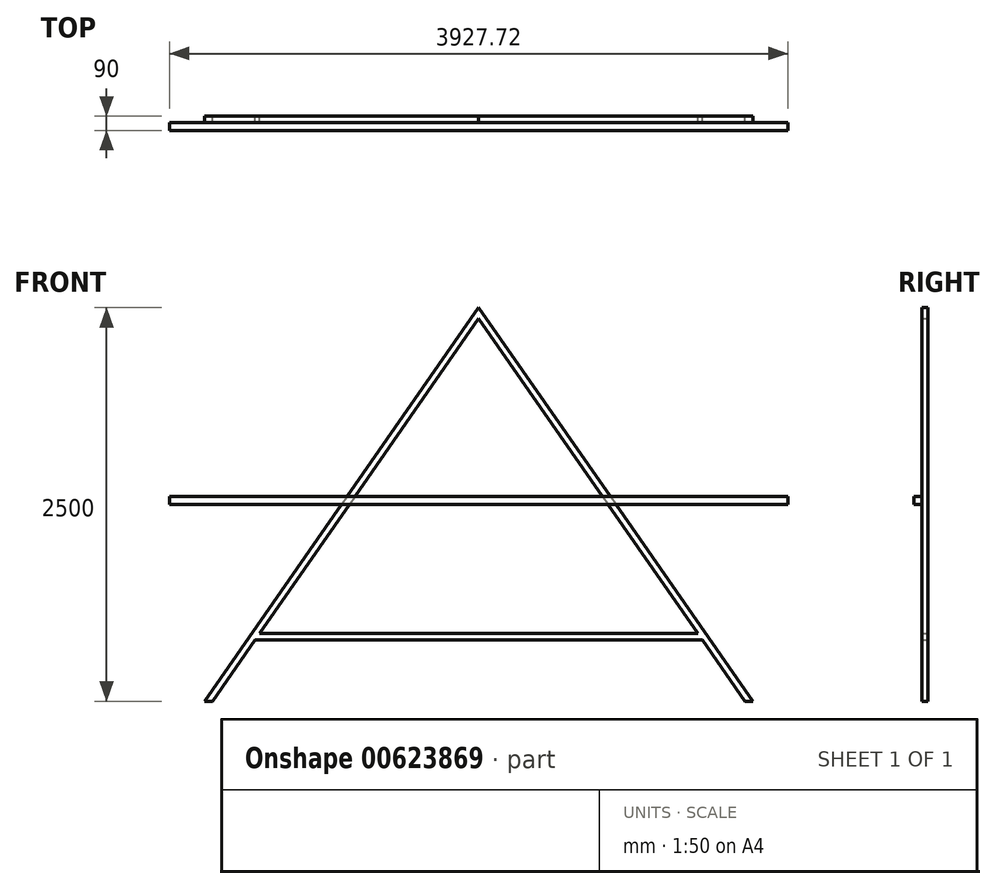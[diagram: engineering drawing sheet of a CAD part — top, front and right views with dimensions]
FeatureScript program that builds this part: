
annotation { "Feature Type Name" : "Feature", "Feature Type Description" : "" }
export const myFeature = defineFeature(function(context is Context, id is Id, definition is map)
    precondition{}
    {
        {
            var Q0;
            Q0=qCreatedBy(makeId("Front.planeOp"),FACE);
            var sketch = newSketch(context, id + "F0", { "sketchPlane" : qUnion([Q0])});
            skLineSegment(sketch, "E0", {"start": v(0, 2500) * mm, "end": v(-1740.78, 0) * mm});
            skLineSegment(sketch, "E1", {"start": v(0, 2500) * mm, "end": v(0, 2430) * mm});
            skLineSegment(sketch, "E2", {"start": v(0, 2430) * mm, "end": v(-1692.03, 0) * mm});
            skLineSegment(sketch, "E3", {"start": v(-1692.03, 0) * mm, "end": v(-1740.78, 0) * mm});
            skLineSegment(sketch, "E4.MirrorCS", {"start": v(1692.03, 0) * mm, "end": v(1740.78, 0) * mm});
            skLineSegment(sketch, "E5.MirrorCS", {"start": v(0, 2500) * mm, "end": v(1740.78, 0) * mm});
            skLineSegment(sketch, "E6.MirrorCS", {"start": v(0, 2430) * mm, "end": v(1692.03, 0) * mm});
            skLineSegment(sketch, "E7", {"start": v(-1392.15, 430.67) * mm, "end": v(1392.15, 430.67) * mm});
            skLineSegment(sketch, "E8", {"start": v(-1420, 390.67) * mm, "end": v(1420, 390.67) * mm});
            skSolve(sketch);
        }
        {
            var Q0;
            {var subQ4=sQuery(id+"F0.wireOp",EDGE,"E3");Q0=makeQuery(id+"F0.imprint","IMPRINT",FACE,{"disambiguationData":[TD([[makeQuery(id+"F0.imprint","IMPRINT",EDGE,{"derivedFrom":subQ4}),-1.0]])]});}
            var Q1;
            {var subQ3=sQuery(id+"F0.wireOp",EDGE,"E4.MirrorCS");Q1=makeQuery(id+"F0.imprint","IMPRINT",FACE,{"disambiguationData":[TD([[makeQuery(id+"F0.imprint","IMPRINT",EDGE,{"derivedFrom":subQ3}),1.0]])]});}
            var Q2;
            {var subQ0=sQuery(id+"F0.wireOp",EDGE,"E7");Q2=makeQuery(id+"F0.imprint","IMPRINT",FACE,{"disambiguationData":[TD([[makeQuery(id+"F0.imprint","IMPRINT",EDGE,{"derivedFrom":subQ0}),-1.0]])]});}
            extrude(context, id + "F1", {"entities" : qUnion([Q0, Q1, Q2]), "depth" : 40 * mm, "offsetDistance" : 25 * mm});
        }
        {
            var Q0;
            Q0=makeQuery(id+"F1.opExtrude","CAP_FACE",FACE,{"disambiguationData":[OSD([sQuery(id+"F0.wireOp",EDGE,"E3"),sQuery(id+"F0.wireOp",EDGE,"E4.MirrorCS"),sQuery(id+"F0.wireOp",EDGE,"E2"),sQuery(id+"F0.wireOp",EDGE,"E5.MirrorCS"),sQuery(id+"F0.wireOp",EDGE,"E6.MirrorCS"),sQuery(id+"F0.wireOp",EDGE,"E0"),sQuery(id+"F0.wireOp",EDGE,"E7"),sQuery(id+"F0.wireOp",EDGE,"E8")])],"isStart":false});
            var sketch = newSketch(context, id + "F2", { "sketchPlane" : qUnion([Q0])});
            skLineSegment(sketch, "E9", {"start": v(-835.57, 1300) * mm, "end": v(-1963.86, 1300) * mm});
            skLineSegment(sketch, "E10", {"start": v(-1963.86, 1300) * mm, "end": v(-1963.86, 1250) * mm});
            skLineSegment(sketch, "E11", {"start": v(-1963.86, 1250) * mm, "end": v(0, 1250) * mm});
            skLineSegment(sketch, "E12", {"start": v(0, 1250) * mm, "end": v(0, 1300) * mm});
            skLineSegment(sketch, "E13", {"start": v(0, 1300) * mm, "end": v(-835.57, 1300) * mm});
            skLineSegment(sketch, "E14.MirrorCS", {"start": v(0, 1300) * mm, "end": v(835.57, 1300) * mm});
            skLineSegment(sketch, "E15.MirrorCS", {"start": v(1963.86, 1250) * mm, "end": v(0, 1250) * mm});
            skLineSegment(sketch, "E16.MirrorCS", {"start": v(1963.86, 1300) * mm, "end": v(1963.86, 1250) * mm});
            skLineSegment(sketch, "E17.MirrorCS", {"start": v(835.57, 1300) * mm, "end": v(1963.86, 1300) * mm});
            skSolve(sketch);
        }
        {
            var Q0;
            {var subQ0=sQuery(id+"F2.wireOp",EDGE,"E9");Q0=makeQuery(id+"F2.imprint","IMPRINT",FACE,{"disambiguationData":[TD([[makeQuery(id+"F2.imprint","IMPRINT",EDGE,{"derivedFrom":subQ0}),1.0]])]});}
            var Q1;
            {var subQ0=sQuery(id+"F2.wireOp",EDGE,"E11");var subQ1=makeQuery(id+"F1.opExtrude","CAP_EDGE",EDGE,{"disambiguationData":[OSD([sQuery(id+"F0.wireOp",EDGE,"E0")])],"isStart":false});var subQ2=makeQuery(id+"F2.imprint","INTERSECT",VERTEX,{"derivedFrom":[subQ1,subQ0]});Q1=makeQuery(id+"F2.imprint","IMPRINT",FACE,{"disambiguationData":[TD([[makeQuery(id+"F2.imprint","IMPRINT",EDGE,{"disambiguationData":[TD([[subQ2,1.0]])],"derivedFrom":subQ1}),1.0]])]});}
            var Q2;
            {var subQ0=sQuery(id+"F2.wireOp",EDGE,"E12");Q2=makeQuery(id+"F2.imprint","IMPRINT",FACE,{"disambiguationData":[TD([[makeQuery(id+"F2.imprint","IMPRINT",EDGE,{"derivedFrom":subQ0}),1.0]])]});}
            var Q3;
            {var subQ0=sQuery(id+"F2.wireOp",EDGE,"E12");Q3=makeQuery(id+"F2.imprint","IMPRINT",FACE,{"disambiguationData":[TD([[makeQuery(id+"F2.imprint","IMPRINT",EDGE,{"derivedFrom":subQ0}),-1.0]])]});}
            var Q4;
            {var subQ1=makeQuery(id+"F1.opExtrude","CAP_EDGE",EDGE,{"disambiguationData":[OSD([sQuery(id+"F0.wireOp",EDGE,"E5.MirrorCS")])],"isStart":false});var subQ6=sQuery(id+"F2.wireOp",EDGE,"E15.MirrorCS");var subQ8=makeQuery(id+"F2.imprint","INTERSECT",VERTEX,{"derivedFrom":[subQ1,subQ6]});Q4=makeQuery(id+"F2.imprint","IMPRINT",FACE,{"disambiguationData":[TD([[makeQuery(id+"F2.imprint","IMPRINT",EDGE,{"disambiguationData":[TD([[subQ8,1.0]])],"derivedFrom":subQ1}),-1.0]])]});}
            var Q5;
            {var subQ0=sQuery(id+"F2.wireOp",EDGE,"E16.MirrorCS");Q5=makeQuery(id+"F2.imprint","IMPRINT",FACE,{"disambiguationData":[TD([[makeQuery(id+"F2.imprint","IMPRINT",EDGE,{"derivedFrom":subQ0}),-1.0]])]});}
            extrude(context, id + "F3", {"entities" : qUnion([Q0, Q1, Q2, Q3, Q4, Q5]), "operationType" : NewBodyOperationType.ADD, "depth" : 50 * mm, "offsetDistance" : 25 * mm});
        }
    });
